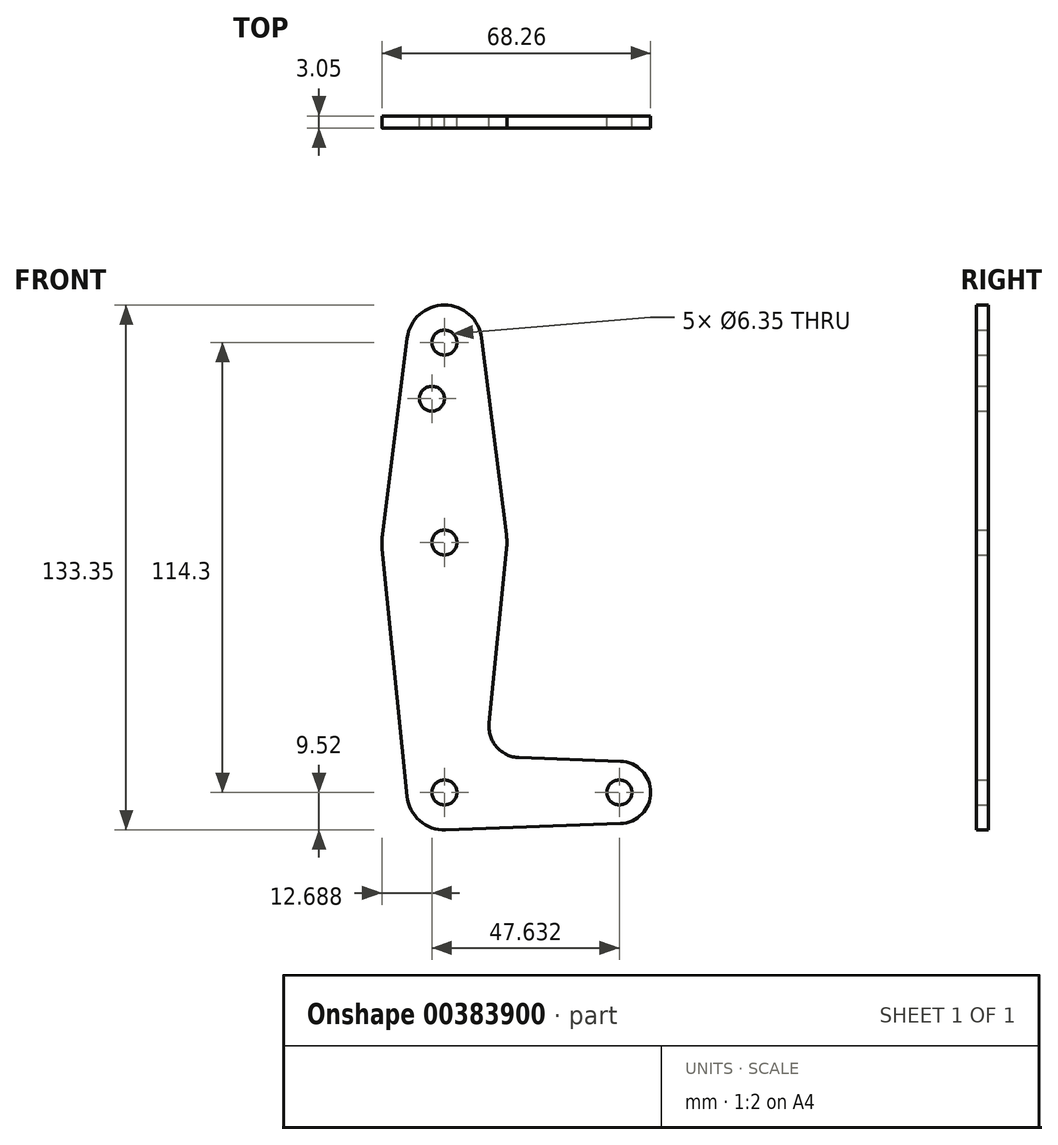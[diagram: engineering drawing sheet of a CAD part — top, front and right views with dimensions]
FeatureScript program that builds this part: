
annotation { "Feature Type Name" : "Feature", "Feature Type Description" : "" }
export const myFeature = defineFeature(function(context is Context, id is Id, definition is map)
    precondition{}
    {
        {
            var Q0;
            Q0=qCreatedBy(makeId("Front.planeOp"),FACE);
            var sketch = newSketch(context, id + "F0", { "sketchPlane" : qUnion([Q0])});
            skLineSegment(sketch, "E0", {"start": v(0, 0) * mm, "end": v(0, 114.3) * mm, "construction": true});
            skLineSegment(sketch, "E1", {"start": v(0, 0) * mm, "end": v(44.45, 0) * mm, "construction": true});
            skCircle(sketch, "E2", {"center": v(0, 114.3) * mm, "radius": 9.53 * mm});
            skCircle(sketch, "E3", {"center": v(0, 0) * mm, "radius": 9.53 * mm});
            skCircle(sketch, "E4", {"center": v(44.45, 0) * mm, "radius": 7.94 * mm});
            skCircle(sketch, "E5", {"center": v(0, 63.5) * mm, "radius": 15.88 * mm});
            skLineSegment(sketch, "E6", {"start": v(9.45, 115.5) * mm, "end": v(15.75, 65.48) * mm});
            skLineSegment(sketch, "E7", {"start": v(-9.45, 115.5) * mm, "end": v(-15.75, 65.48) * mm});
            skLineSegment(sketch, "E8", {"start": v(-15.8, 61.91) * mm, "end": v(-9.48, -0.95) * mm});
            skLineSegment(sketch, "E9", {"start": v(15.8, 61.91) * mm, "end": v(11.34, 17.6) * mm});
            skLineSegment(sketch, "E10", {"start": v(18.97, 8.85) * mm, "end": v(44.73, 7.93) * mm});
            skLineSegment(sketch, "E11", {"start": v(0.34, -9.52) * mm, "end": v(44.73, -7.93) * mm});
            skArc(sketch, "E12.filletArc", {"start": v(11.34, 17.6) * mm, "mid": v(13.26, 11.57) * mm, "end": v(18.97, 8.85) * mm});
            skCircle(sketch, "E13", {"center": v(0, 114.3) * mm, "radius": 3.18 * mm});
            skCircle(sketch, "E14", {"center": v(0, 63.5) * mm, "radius": 3.18 * mm});
            skCircle(sketch, "E15", {"center": v(0, 0) * mm, "radius": 3.18 * mm});
            skCircle(sketch, "E16", {"center": v(44.45, 0) * mm, "radius": 3.18 * mm});
            skCircle(sketch, "E17", {"center": v(-3.18, 100.03) * mm, "radius": 3.18 * mm});
            skSolve(sketch);
        }
        {
            var Q0;
            Q0 = qSketchRegion(id + "F0", true);
            extrude(context, id + "F1", {"entities" : qUnion([Q0]), "depth" : 3.05 * mm});
        }
    });
